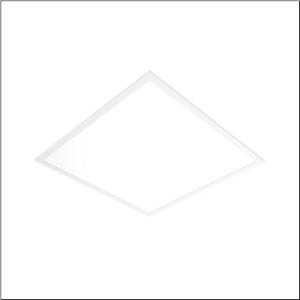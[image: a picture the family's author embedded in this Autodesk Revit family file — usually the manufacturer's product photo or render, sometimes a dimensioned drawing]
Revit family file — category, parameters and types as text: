
# Revit family: apollon_r__41_51mh12wd2443_fb74
name_source: partatom
category: Lighting Fixtures
units: mm (PartAtom-declared; Revit-internal decimal feet)

## family parameters
Cut with Voids When Loaded = No
Host = Face
Light Source = No
Part Type = Normal
Room Calculation Point = No
Round Connector Dimension = Use Diameter
Shared = No

## types (1)
- Apollon® 41 (1 x LED, 3500 lm, 28.5 W, 4000K)
    Apparent Load = 29 VA
    CIE Flux Codes = 61 87 97 100 100
    Color Rendering = 80
    Color Temperature = 4000K
    Default Elevation = 1800 mm
    Description = Apollon® 41, office luminaire, primary optical cover: prismatic diffuser, of PS, light emission: direct distribution, primary light characteristic: symmetric, installation type: lay-in mounting, LED, rated luminous flux: 3.500lm, luminous efficacy: 123lm/W, light colour: 840, colour temperature: 4000K, with terminal, 5-pole, mains connection: 220..240V, AC/DC, 0/50..60Hz, housing, of aluminium section, traffic white (RAL 9016), module: M600, length: 600mm, width: 600mm, height: 28mm, housing upper side, of sheet steel, protection rating (complete): IP20, protection rating (lamp compartment, on room side): IP40, insulation class (complete): insulation class II (safety insulation), certification: CE, ENEC, permissible operating ambient temperature: -25..+40°C, packaging unit: 1 piece
    Height = 0 mm  [stored 0 ft]
    Lamp = 1 x LED
    Lamp Light Flux = 3500 lm
    Lamp Power = 28.5 W
    Lamp count = 1
    Length = 600 mm
    Luminous efficacy = 123 lm/W
    Manufacturer = Siteco
    ModVariant = No
    Model = 51MH12WD2443
    Mounting Place = Ceiling
    Mounting Type = Recessed
    Number of Poles = 1
    OnlyDefault = Yes
    Power Factor = 1
    Product Name = Apollon® 41
    Product group = office luminaire | ceiling recessed
    ProductGroupID = 400
    Protection Class = Protection class II
    Protection Degree = IP 20
    RLX_Detail_Level = 1
    RLX_Emergency_Light_Flux = 0 lm
    RLX_Emergency_Type = 0
    RLX_Emergency_Type_DB = No
    RlxData = <blob elided: 12193 chars, md5=43c087da>
    Socket = socket
    Standby Power = 0 W
    System Light Flux = 3500 lm
    System Power = 29 W
    Type Comments = Product without accessories
    Type Image = l_1291024.jpg
    URL = http://relux.com
    VarID = ---
    Voltage = 0 V
    Weight = 0.00 kg
    Width = 600 mm

note: [stored X ft] marks values corroborated as IEEE doubles in the binary element streams (Revit-internal decimal feet)

## geometry (parser evidence)
native form markers: Sweep x10
no freeform markers — native parametric forms only
